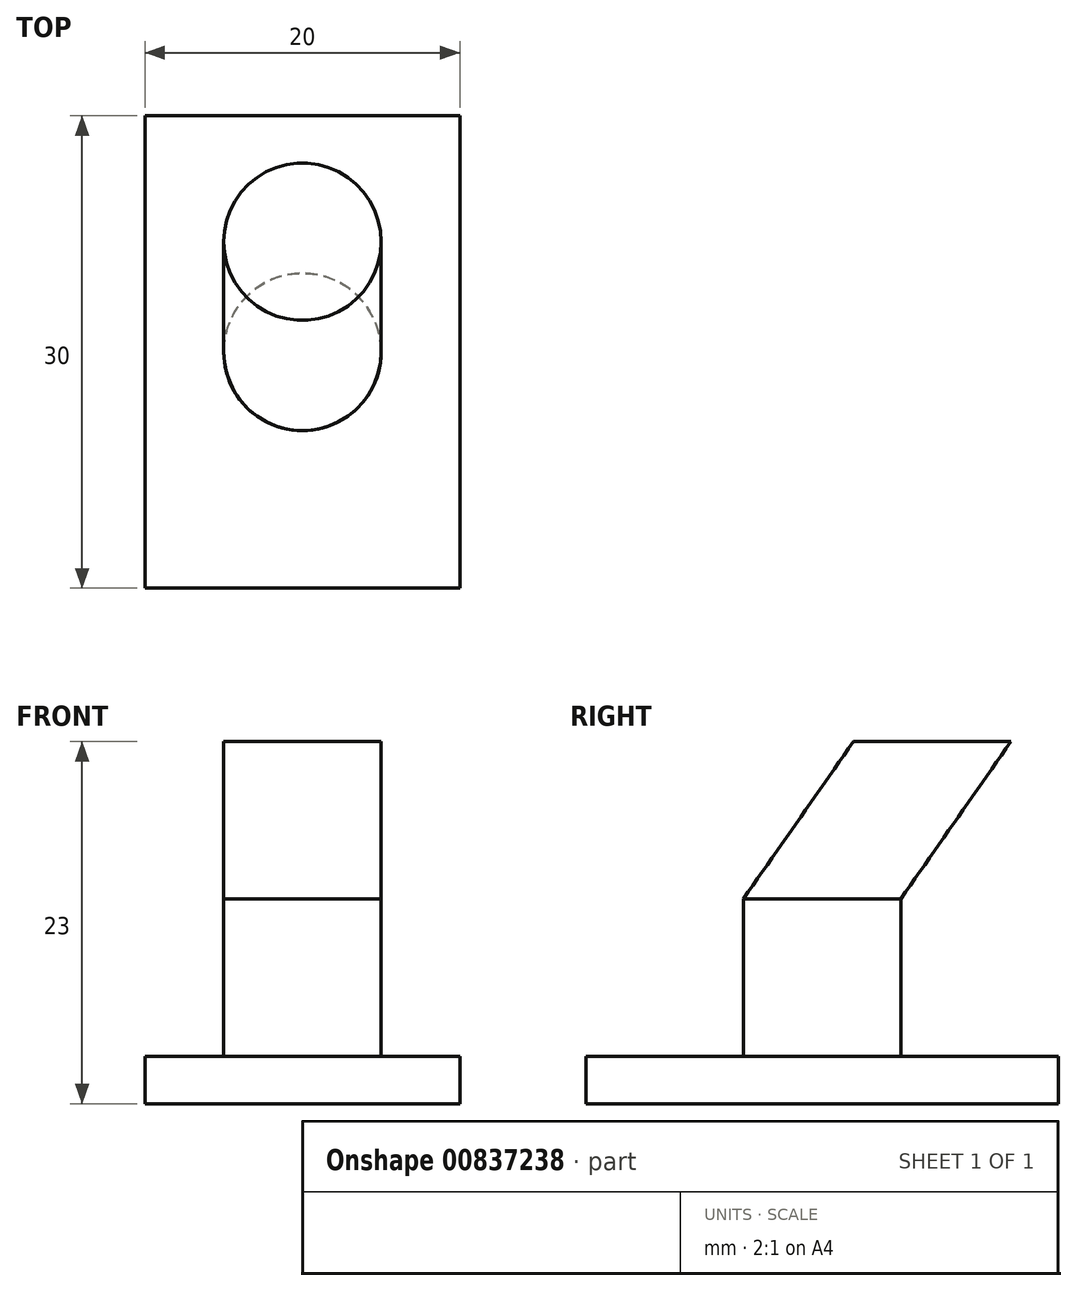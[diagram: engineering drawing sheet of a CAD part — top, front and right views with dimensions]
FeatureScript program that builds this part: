
annotation { "Feature Type Name" : "Feature", "Feature Type Description" : "" }
export const myFeature = defineFeature(function(context is Context, id is Id, definition is map)
    precondition{}
    {
        {
            var Q0;
            Q0=qCreatedBy(makeId("Top.planeOp"),FACE);
            var sketch = newSketch(context, id + "F0", { "sketchPlane" : qUnion([Q0])});
            skLineSegment(sketch, "E0.bottom", {"start": v(10, -15) * mm, "end": v(-10, -15) * mm});
            skLineSegment(sketch, "E0.top", {"start": v(10, 15) * mm, "end": v(-10, 15) * mm});
            skLineSegment(sketch, "E0.left", {"start": v(10, -15) * mm, "end": v(10, 15) * mm});
            skLineSegment(sketch, "E0.right", {"start": v(-10, -15) * mm, "end": v(-10, 15) * mm});
            skPoint(sketch, "E0.middle", {"position": v(0, 0) * mm});
            skSolve(sketch);
        }
        {
            var Q0;
            Q0=makeQuery(id+"F0.imprint","IMPRINT",FACE,{"disambiguationData":[TD([[makeQuery(id+"F0.imprint","IMPRINT",EDGE,{"derivedFrom":sQuery(id+"F0.wireOp",EDGE,"E0.bottom")}),-1.0]])]});
            extrude(context, id + "F1", {"entities" : qUnion([Q0]), "depth" : 3 * mm, "offsetDistance" : 25 * mm});
        }
        {
            var Q0;
            Q0=makeQuery(id+"F1.opExtrude","CAP_FACE",FACE,{"disambiguationData":[OSD([sQuery(id+"F0.wireOp",EDGE,"E0.bottom"),sQuery(id+"F0.wireOp",EDGE,"E0.top"),sQuery(id+"F0.wireOp",EDGE,"E0.left"),sQuery(id+"F0.wireOp",EDGE,"E0.right")])],"isStart":false});
            var sketch = newSketch(context, id + "F2", { "sketchPlane" : qUnion([Q0])});
            skCircle(sketch, "E1", {"center": v(0, 0) * mm, "radius": 5 * mm});
            skSolve(sketch);
        }
        {
            var Q0;
            Q0=makeQuery(id+"F2.imprint","IMPRINT",FACE,{"disambiguationData":[TD([[makeQuery(id+"F2.imprint","IMPRINT",EDGE,{"derivedFrom":sQuery(id+"F2.wireOp",EDGE,"E1")}),1.0]])]});
            extrude(context, id + "F3", {"entities" : qUnion([Q0]), "operationType" : NewBodyOperationType.ADD, "depth" : 10 * mm, "offsetDistance" : 25 * mm});
        }
        {
            var Q0;
            Q0=makeQuery(id+"F3.opExtrude","CAP_FACE",FACE,{"disambiguationData":[OSD([sQuery(id+"F2.wireOp",EDGE,"E1")])],"isStart":false});
            cPlane(context, id + "F4", {"entities" : qUnion([Q0]), "cplaneType" : CPlaneType.OFFSET, "offset" : 10 * mm, "width" : 150 * mm, "height" : 150 * mm});
        }
        {
            var Q0;
            Q0=qCreatedBy(id+"F4.planeOp",FACE);
            var sketch = newSketch(context, id + "F5", { "sketchPlane" : qUnion([Q0])});
            skPoint(sketch, "E2.0", {"position": v(0, 0) * mm});
            skLineSegment(sketch, "E3", {"start": v(0, 0) * mm, "end": v(0, 7) * mm, "construction": true});
            skCircle(sketch, "E4", {"center": v(0, 7) * mm, "radius": 1 * mm});
            skSolve(sketch);
        }
        {
            var Q0;
            Q0=makeQuery(id+"F3.opExtrude","CAP_FACE",FACE,{"disambiguationData":[OSD([sQuery(id+"F2.wireOp",EDGE,"E1")])],"isStart":false});
            var sketch = newSketch(context, id + "F6", { "sketchPlane" : qUnion([Q0])});
            skPoint(sketch, "E5.0", {"position": v(0, 0) * mm});
            skSolve(sketch);
        }
        {
            var Q0;
            Q0=sQuery(id+"F6.wireOp",VERTEX,"E5.0");
            var Q1;
            Q1=sQuery(id+"F5.wireOp",VERTEX,"E2.0");
            var Q2;
            Q2=sQuery(id+"F5.wireOp",VERTEX,"E3.end");
            cPlane(context, id + "F7", {"entities" : qUnion([Q0, Q1, Q2]), "cplaneType" : CPlaneType.THREE_POINT, "offset" : 25 * mm, "width" : 150 * mm, "height" : 150 * mm});
        }
        {
            var Q0;
            Q0=qCreatedBy(id+"F7.planeOp",FACE);
            var sketch = newSketch(context, id + "F8", { "sketchPlane" : qUnion([Q0])});
            skPoint(sketch, "E6.0", {"position": v(0, 13) * mm});
            skPoint(sketch, "E7.0", {"position": v(7, 23) * mm});
            skLineSegment(sketch, "E8", {"start": v(0, 13) * mm, "end": v(7, 23) * mm});
            skSolve(sketch);
        }
        {
            var Q0;
            Q0=makeQuery(id+"F6.imprint","IMPRINT",FACE,{"disambiguationData":[TD([[makeQuery(id+"F6.imprint","IMPRINT",EDGE,{"derivedFrom":makeQuery(id+"F3.opExtrude","CAP_EDGE",EDGE,{"disambiguationData":[OSD([sQuery(id+"F2.wireOp",EDGE,"E1")])],"isStart":false})}),1.0]])]});
            var Q1;
            Q1=sQuery(id+"F8.wireOp",EDGE,"E8");
            sweep(context, id + "F9", {"operationType" : NewBodyOperationType.ADD, "profiles" : qUnion([Q0]), "path" : qUnion([Q1])});
        }
    });
